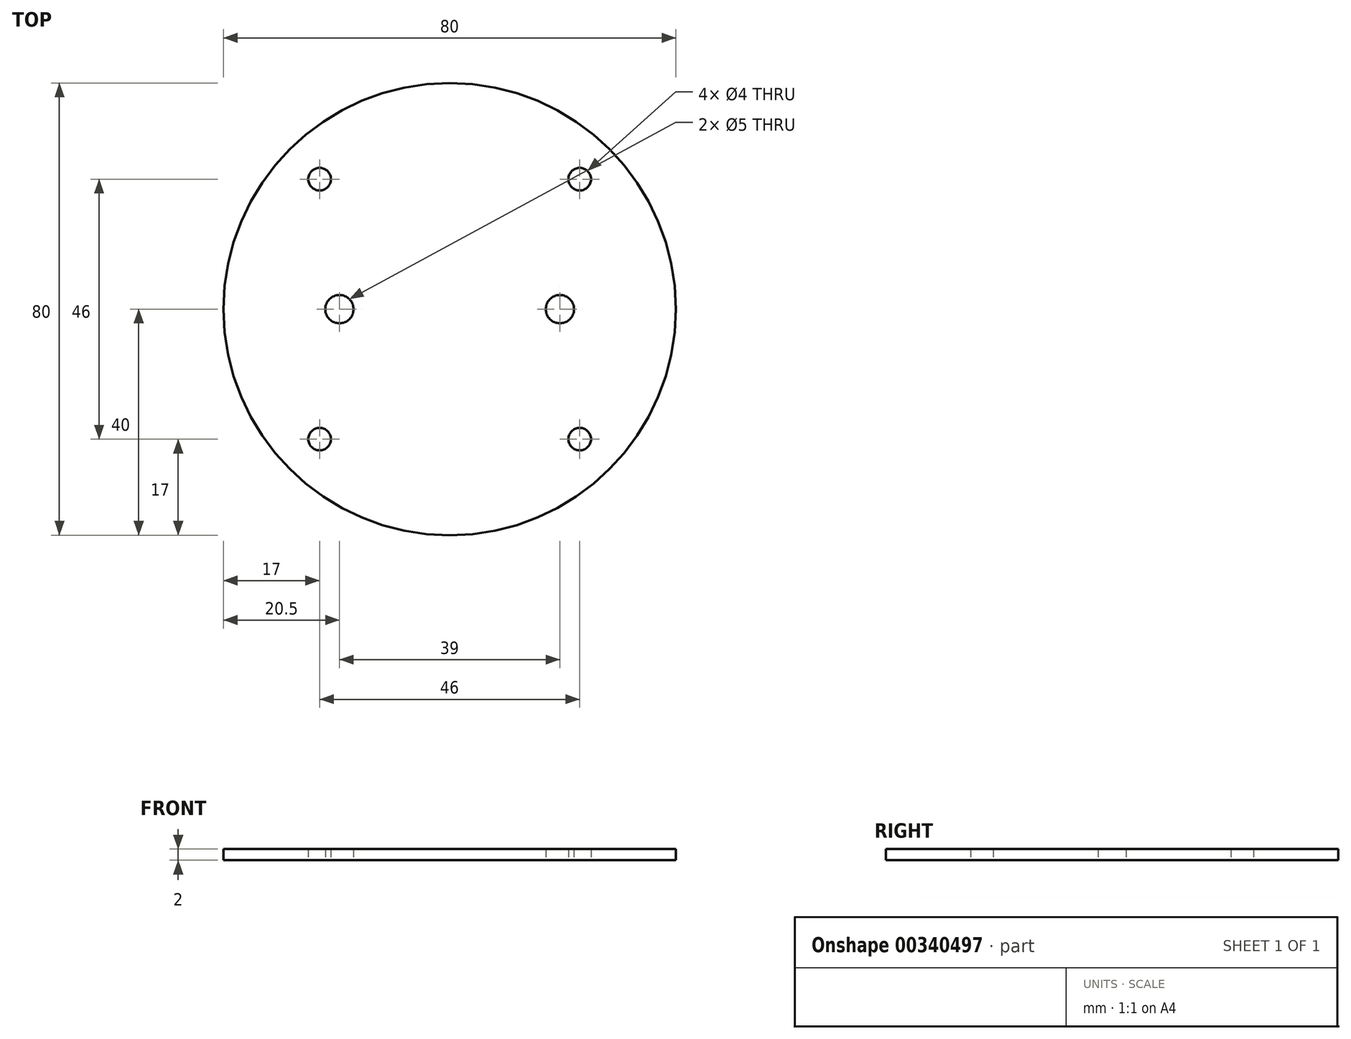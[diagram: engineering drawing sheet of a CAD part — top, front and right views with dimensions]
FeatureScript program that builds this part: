
annotation { "Feature Type Name" : "Feature", "Feature Type Description" : "" }
export const myFeature = defineFeature(function(context is Context, id is Id, definition is map)
    precondition{}
    {
        {
            var Q0;
            Q0=qCreatedBy(makeId("Top.planeOp"),FACE);
            var sketch = newSketch(context, id + "F0", { "sketchPlane" : qUnion([Q0])});
            skCircle(sketch, "E0", {"center": v(0, 0) * mm, "radius": 40 * mm});
            skCircle(sketch, "E1", {"center": v(-23, 23) * mm, "radius": 2 * mm});
            skCircle(sketch, "E2", {"center": v(23, 23) * mm, "radius": 2 * mm});
            skCircle(sketch, "E3", {"center": v(-23, -23) * mm, "radius": 2 * mm});
            skCircle(sketch, "E4", {"center": v(23, -23) * mm, "radius": 2 * mm});
            skLineSegment(sketch, "E5", {"start": v(-19.5, 0) * mm, "end": v(19.5, 0) * mm});
            skCircle(sketch, "E6", {"center": v(-19.5, 0) * mm, "radius": 2.5 * mm});
            skCircle(sketch, "E7", {"center": v(19.5, 0) * mm, "radius": 2.5 * mm});
            skSolve(sketch);
        }
        {
            var Q0;
            Q0=qSketchRegion(id+"F0",true);
            extrude(context, id + "F1", {"entities" : qUnion([Q0]), "depth" : 2 * mm});
        }
    });
